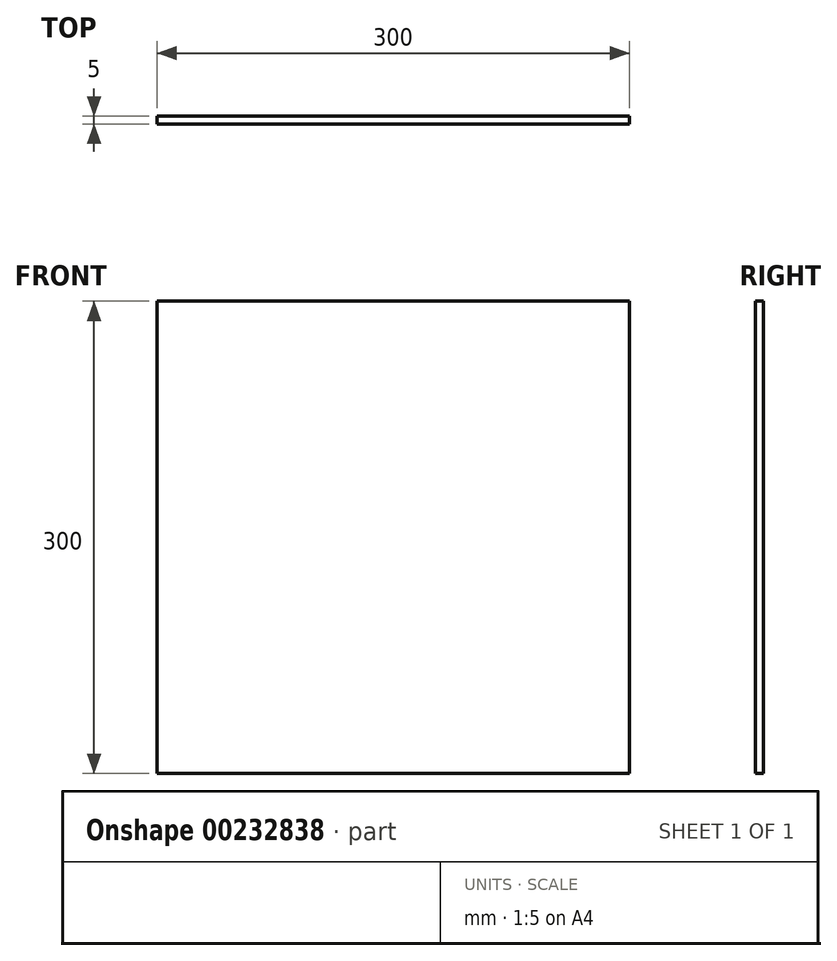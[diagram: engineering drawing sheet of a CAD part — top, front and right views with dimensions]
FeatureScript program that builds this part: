
annotation { "Feature Type Name" : "Feature", "Feature Type Description" : "" }
export const myFeature = defineFeature(function(context is Context, id is Id, definition is map)
    precondition{}
    {
        {
            var Q0;
            Q0=qCreatedBy(makeId("Front.planeOp"),FACE);
            var sketch = newSketch(context, id + "F0", { "sketchPlane" : qUnion([Q0])});
            skLineSegment(sketch, "E0.bottom", {"start": v(-151.69, 211.57) * mm, "end": v(148.31, 211.57) * mm});
            skLineSegment(sketch, "E0.top", {"start": v(-151.69, -88.43) * mm, "end": v(148.31, -88.43) * mm});
            skLineSegment(sketch, "E0.left", {"start": v(-151.69, 211.57) * mm, "end": v(-151.69, -88.43) * mm});
            skLineSegment(sketch, "E0.right", {"start": v(148.31, 211.57) * mm, "end": v(148.31, -88.43) * mm});
            skSolve(sketch);
        }
        {
            var Q0;
            Q0=makeQuery(id+"F0.imprint","IMPRINT",FACE,{"disambiguationData":[TD([[makeQuery(id+"F0.imprint","IMPRINT",EDGE,{"derivedFrom":sQuery(id+"F0.wireOp",EDGE,"E0.bottom")}),-1.0]])]});
            extrude(context, id + "F1", {"entities" : qUnion([Q0]), "depth" : 5 * mm});
        }
    });
